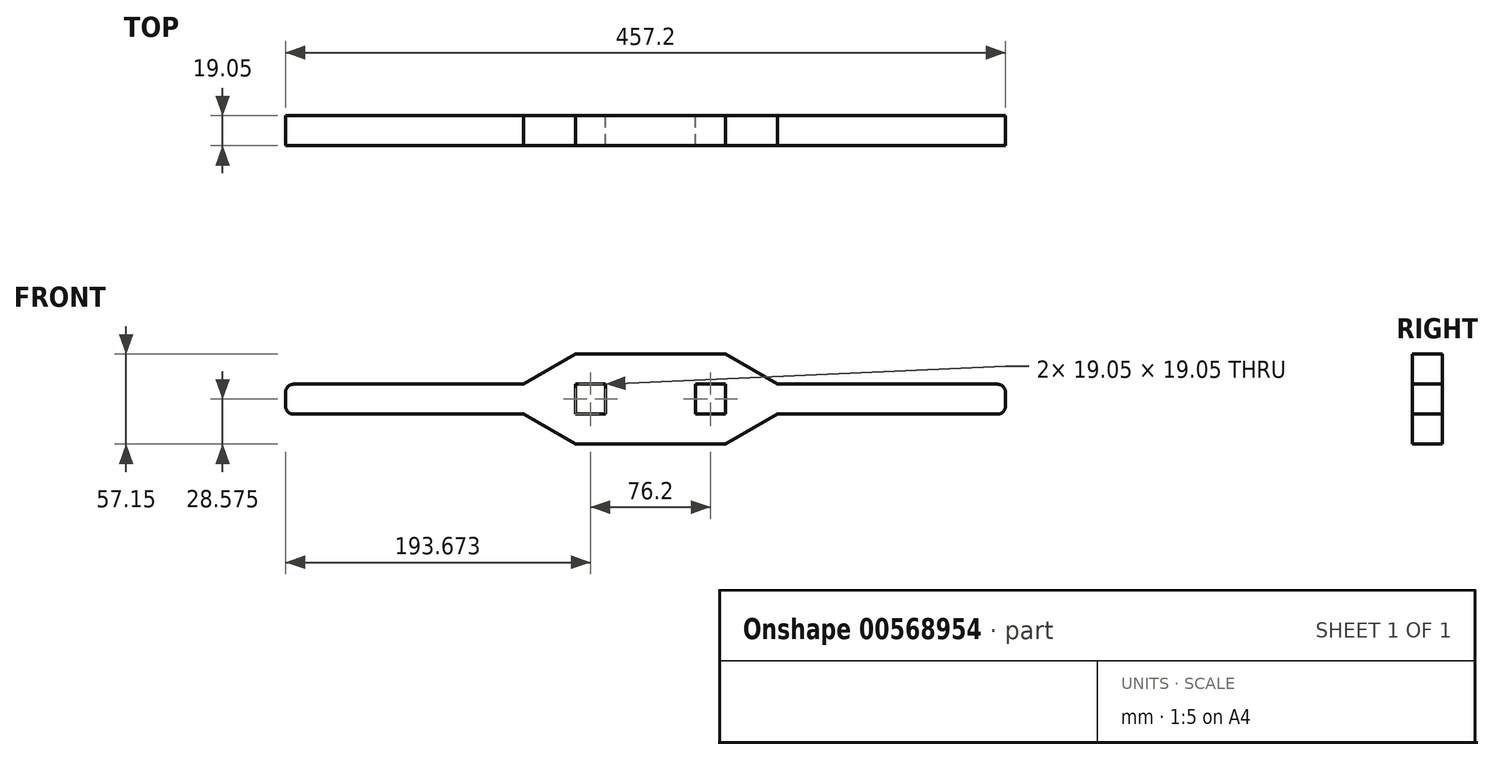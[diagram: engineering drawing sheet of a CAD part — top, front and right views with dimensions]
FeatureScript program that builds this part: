
annotation { "Feature Type Name" : "Feature", "Feature Type Description" : "" }
export const myFeature = defineFeature(function(context is Context, id is Id, definition is map)
    precondition{}
    {
        {
            var Q0;
            Q0=qCreatedBy(makeId("Front.planeOp"),FACE);
            var sketch = newSketch(context, id + "F0", { "sketchPlane" : qUnion([Q0])});
            skLineSegment(sketch, "E0.bottom", {"start": v(-147.65, 19.05) * mm, "end": v(309.55, 19.05) * mm});
            skLineSegment(sketch, "E0.top", {"start": v(-147.65, 0) * mm, "end": v(309.55, 0) * mm});
            skLineSegment(sketch, "E0.left", {"start": v(-147.65, 19.05) * mm, "end": v(-147.65, 0) * mm});
            skLineSegment(sketch, "E0.right", {"start": v(309.55, 19.05) * mm, "end": v(309.55, 0) * mm});
            skLineSegment(sketch, "E1", {"start": v(80.95, 19.05) * mm, "end": v(80.95, 0) * mm});
            skLineSegment(sketch, "E2.bottom", {"start": v(36.5, 19.05) * mm, "end": v(55.55, 19.05) * mm});
            skLineSegment(sketch, "E2.top", {"start": v(36.5, 0) * mm, "end": v(55.55, 0) * mm});
            skLineSegment(sketch, "E2.left", {"start": v(36.5, 19.05) * mm, "end": v(36.5, 0) * mm});
            skLineSegment(sketch, "E2.right", {"start": v(55.55, 19.05) * mm, "end": v(55.55, 0) * mm});
            skLineSegment(sketch, "E3.bottom", {"start": v(112.7, 19.05) * mm, "end": v(131.75, 19.05) * mm});
            skLineSegment(sketch, "E3.top", {"start": v(112.7, 0) * mm, "end": v(131.75, 0) * mm});
            skLineSegment(sketch, "E3.left", {"start": v(112.7, 19.05) * mm, "end": v(112.7, 0) * mm});
            skLineSegment(sketch, "E3.right", {"start": v(131.75, 19.05) * mm, "end": v(131.75, 0) * mm});
            skLineSegment(sketch, "E4", {"start": v(36.5, 9.52) * mm, "end": v(55.55, 9.52) * mm});
            skLineSegment(sketch, "E5", {"start": v(112.7, 9.52) * mm, "end": v(131.75, 9.52) * mm});
            skCircle(sketch, "E6", {"center": v(46.02, 9.52) * mm, "radius": 6.35 * mm});
            skCircle(sketch, "E7", {"center": v(122.22, 9.52) * mm, "radius": 6.35 * mm});
            skLineSegment(sketch, "E8.top", {"start": v(36.5, 38.1) * mm, "end": v(55.55, 38.1) * mm});
            skLineSegment(sketch, "E8.left", {"start": v(36.5, 19.05) * mm, "end": v(36.5, 38.1) * mm});
            skLineSegment(sketch, "E8.right", {"start": v(55.55, 19.05) * mm, "end": v(55.55, 38.1) * mm});
            skLineSegment(sketch, "E9.top", {"start": v(36.5, -19.05) * mm, "end": v(55.55, -19.05) * mm});
            skLineSegment(sketch, "E9.left", {"start": v(36.5, 0) * mm, "end": v(36.5, -19.05) * mm});
            skLineSegment(sketch, "E9.right", {"start": v(55.55, 0) * mm, "end": v(55.55, -19.05) * mm});
            skLineSegment(sketch, "E10.top", {"start": v(112.7, 38.1) * mm, "end": v(131.75, 38.1) * mm});
            skLineSegment(sketch, "E10.left", {"start": v(112.7, 19.05) * mm, "end": v(112.7, 38.1) * mm});
            skLineSegment(sketch, "E10.right", {"start": v(131.75, 19.05) * mm, "end": v(131.75, 38.1) * mm});
            skLineSegment(sketch, "E11.top", {"start": v(112.7, -19.05) * mm, "end": v(131.75, -19.05) * mm});
            skLineSegment(sketch, "E11.left", {"start": v(112.7, 0) * mm, "end": v(112.7, -19.05) * mm});
            skLineSegment(sketch, "E11.right", {"start": v(131.75, 0) * mm, "end": v(131.75, -19.05) * mm});
            skLineSegment(sketch, "E12", {"start": v(36.5, 38.1) * mm, "end": v(3.5, 19.05) * mm});
            skLineSegment(sketch, "E13", {"start": v(55.55, 38.1) * mm, "end": v(112.7, 38.1) * mm});
            skLineSegment(sketch, "E14", {"start": v(131.75, 38.1) * mm, "end": v(164.74, 19.05) * mm});
            skLineSegment(sketch, "E15", {"start": v(55.55, -19.05) * mm, "end": v(112.7, -19.05) * mm});
            skLineSegment(sketch, "E16", {"start": v(36.5, -19.05) * mm, "end": v(3.5, 0) * mm});
            skLineSegment(sketch, "E17", {"start": v(131.75, -19.05) * mm, "end": v(164.74, 0) * mm});
            skSolve(sketch);
        }
        {
            var Q0;
            Q0 = qSketchRegion(id + "F0", true);
            var Q1;
            {var subQ0=sQuery(id+"F0.wireOp",EDGE,"E1");Q1=makeQuery(id+"F0.imprint","IMPRINT",FACE,{"disambiguationData":[TD([[makeQuery(id+"F0.imprint","IMPRINT",EDGE,{"derivedFrom":subQ0}),-1.0]])]});}
            var Q2;
            {var subQ4=sQuery(id+"F0.wireOp",EDGE,"E1");Q2=makeQuery(id+"F0.imprint","IMPRINT",FACE,{"disambiguationData":[TD([[makeQuery(id+"F0.imprint","IMPRINT",EDGE,{"derivedFrom":subQ4}),1.0]])]});}
            var Q3;
            {var subQ8=sQuery(id+"F0.wireOp",EDGE,"E3.top");Q3=makeQuery(id+"F0.imprint","IMPRINT",FACE,{"disambiguationData":[TD([[makeQuery(id+"F0.imprint","IMPRINT",EDGE,{"derivedFrom":subQ8}),1.0]])]});}
            var Q4;
            {var subQ5=sQuery(id+"F0.wireOp",EDGE,"E2.bottom");Q4=makeQuery(id+"F0.imprint","IMPRINT",FACE,{"disambiguationData":[TD([[makeQuery(id+"F0.imprint","IMPRINT",EDGE,{"derivedFrom":subQ5}),-1.0]])]});}
            var Q5;
            {var subQ8=sQuery(id+"F0.wireOp",EDGE,"E2.top");Q5=makeQuery(id+"F0.imprint","IMPRINT",FACE,{"disambiguationData":[TD([[makeQuery(id+"F0.imprint","IMPRINT",EDGE,{"derivedFrom":subQ8}),1.0]])]});}
            var Q6;
            {var subQ8=sQuery(id+"F0.wireOp",EDGE,"E3.bottom");Q6=makeQuery(id+"F0.imprint","IMPRINT",FACE,{"disambiguationData":[TD([[makeQuery(id+"F0.imprint","IMPRINT",EDGE,{"derivedFrom":subQ8}),-1.0]])]});}
            extrude(context, id + "F1", {"entities" : qUnion([Q0, Q1, Q2, Q3, Q4, Q5, Q6]), "depth" : 19.05 * mm, "offsetDistance" : 25.4 * mm});
        }
        {
            var Q0;
            Q0=makeQuery(id+"F1.opExtrude","SWEPT_EDGE",EDGE,{"disambiguationData":[OSD([sQuery(id+"F0.wireOp",EDGE,"E0.bottom"),sQuery(id+"F0.wireOp",EDGE,"E0.right")])]});
            var Q1;
            Q1=makeQuery(id+"F1.opExtrude","SWEPT_EDGE",EDGE,{"disambiguationData":[OSD([sQuery(id+"F0.wireOp",EDGE,"E0.top"),sQuery(id+"F0.wireOp",EDGE,"E0.right")])]});
            var Q2;
            Q2=makeQuery(id+"F1.opExtrude","SWEPT_EDGE",EDGE,{"disambiguationData":[OSD([sQuery(id+"F0.wireOp",EDGE,"E0.bottom"),sQuery(id+"F0.wireOp",EDGE,"E0.left")])]});
            var Q3;
            Q3=makeQuery(id+"F1.opExtrude","SWEPT_EDGE",EDGE,{"disambiguationData":[OSD([sQuery(id+"F0.wireOp",EDGE,"E0.top"),sQuery(id+"F0.wireOp",EDGE,"E0.left")])]});
            fillet(context, id + "F2", {"entities" : qUnion([Q0, Q1, Q2, Q3]), "radius" : 5.08 * mm, "tangentPropagation" : true, "allowEdgeOverflow" : false});
        }
    });
